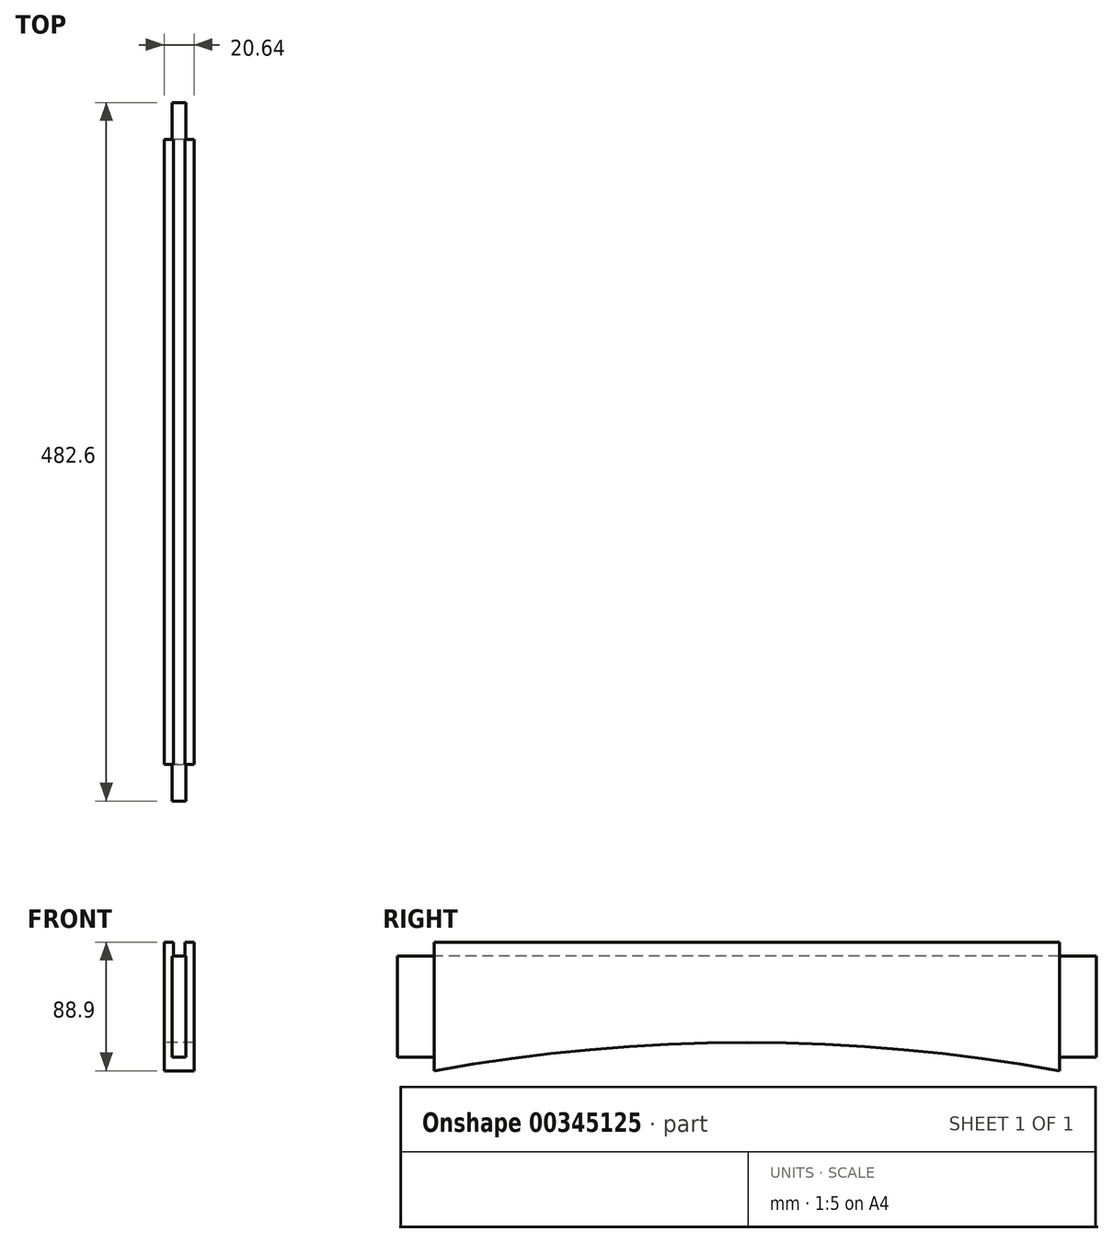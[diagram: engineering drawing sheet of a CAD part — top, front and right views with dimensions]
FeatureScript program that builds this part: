
annotation { "Feature Type Name" : "Feature", "Feature Type Description" : "" }
export const myFeature = defineFeature(function(context is Context, id is Id, definition is map)
    precondition{}
    {
        {
            var Q0;
            Q0=qCreatedBy(makeId("Right.planeOp"),FACE);
            var sketch = newSketch(context, id + "F0", { "sketchPlane" : qUnion([Q0])});
            skLineSegment(sketch, "E0.bottom", {"start": v(-215.9, 44.45) * mm, "end": v(215.9, 44.45) * mm});
            skLineSegment(sketch, "E0.top", {"start": v(-215.9, -44.45) * mm, "end": v(215.9, -44.45) * mm});
            skLineSegment(sketch, "E0.left", {"start": v(-215.9, 44.45) * mm, "end": v(-215.9, -44.45) * mm});
            skLineSegment(sketch, "E0.right", {"start": v(215.9, 44.45) * mm, "end": v(215.9, -44.45) * mm});
            skPoint(sketch, "E0.middle", {"position": v(0, 0) * mm});
            skPoint(sketch, "E1", {"position": v(0, -1232.92) * mm});
            skArc(sketch, "E2", {"start": v(-215.9, -44.45) * mm, "mid": v(0, -25) * mm, "end": v(215.9, -44.45) * mm});
            skSolve(sketch);
        }
        {
            var Q0;
            Q0=makeQuery(id+"F0.imprint","IMPRINT",FACE,{"disambiguationData":[TD([[makeQuery(id+"F0.imprint","IMPRINT",EDGE,{"derivedFrom":sQuery(id+"F0.wireOp",EDGE,"E0.bottom")}),-1.0]])]});
            extrude(context, id + "F1", {"entities" : qUnion([Q0]), "endBound" : BoundingType.SYMMETRIC, "depth" : 20.64 * mm});
        }
        {
            var Q0;
            Q0=makeQuery(id+"F1.opExtrude","SWEPT_FACE",FACE,{"disambiguationData":[OSD([sQuery(id+"F0.wireOp",EDGE,"E0.left")])]});
            var sketch = newSketch(context, id + "F2", { "sketchPlane" : qUnion([Q0])});
            skLineSegment(sketch, "E3.bottom", {"start": v(-4.76, 34.92) * mm, "end": v(4.76, 34.92) * mm});
            skLineSegment(sketch, "E3.top", {"start": v(-4.76, -34.92) * mm, "end": v(4.76, -34.92) * mm});
            skLineSegment(sketch, "E3.left", {"start": v(-4.76, 34.92) * mm, "end": v(-4.76, -34.92) * mm});
            skLineSegment(sketch, "E3.right", {"start": v(4.76, 34.92) * mm, "end": v(4.76, -34.92) * mm});
            skPoint(sketch, "E3.middle", {"position": v(0, 0) * mm});
            skSolve(sketch);
        }
        {
            var Q0;
            Q0 = qSketchRegion(id + "F2", true);
            extrude(context, id + "F3", {"entities" : qUnion([Q0]), "operationType" : NewBodyOperationType.ADD, "depth" : 25.4 * mm});
        }
        {
            var Q0;
            Q0=makeQuery(id+"F1.opExtrude","SWEPT_FACE",FACE,{"disambiguationData":[OSD([sQuery(id+"F0.wireOp",EDGE,"E0.right")])]});
            var sketch = newSketch(context, id + "F4", { "sketchPlane" : qUnion([Q0])});
            skLineSegment(sketch, "E4.bottom", {"start": v(-4.76, 34.93) * mm, "end": v(4.76, 34.93) * mm});
            skLineSegment(sketch, "E4.top", {"start": v(-4.76, -34.93) * mm, "end": v(4.76, -34.93) * mm});
            skLineSegment(sketch, "E4.left", {"start": v(-4.76, 34.92) * mm, "end": v(-4.76, -34.92) * mm});
            skLineSegment(sketch, "E4.right", {"start": v(4.76, 34.92) * mm, "end": v(4.76, -34.92) * mm});
            skPoint(sketch, "E4.middle", {"position": v(0, 0) * mm});
            skSolve(sketch);
        }
        {
            var Q0;
            Q0 = qSketchRegion(id + "F4", true);
            extrude(context, id + "F5", {"entities" : qUnion([Q0]), "operationType" : NewBodyOperationType.ADD, "depth" : 25.4 * mm});
        }
        {
            var Q0;
            Q0=makeQuery(id+"F1.opExtrude","SWEPT_FACE",FACE,{"disambiguationData":[OSD([sQuery(id+"F0.wireOp",EDGE,"E0.bottom")])]});
            var sketch = newSketch(context, id + "F6", { "sketchPlane" : qUnion([Q0])});
            skLineSegment(sketch, "E5.bottom", {"start": v(3.97, 215.9) * mm, "end": v(-3.97, 215.9) * mm});
            skLineSegment(sketch, "E5.top", {"start": v(3.97, -215.9) * mm, "end": v(-3.97, -215.9) * mm});
            skLineSegment(sketch, "E5.left", {"start": v(3.97, 215.9) * mm, "end": v(3.97, -215.9) * mm});
            skLineSegment(sketch, "E5.right", {"start": v(-3.97, 215.9) * mm, "end": v(-3.97, -215.9) * mm});
            skPoint(sketch, "E5.middle", {"position": v(0, 0) * mm});
            skSolve(sketch);
        }
        {
            var Q0;
            Q0 = qSketchRegion(id + "F6", true);
            extrude(context, id + "F7", {"entities" : qUnion([Q0]), "operationType" : NewBodyOperationType.REMOVE, "oppositeDirection" : true, "depth" : 9.52 * mm});
        }
    });
